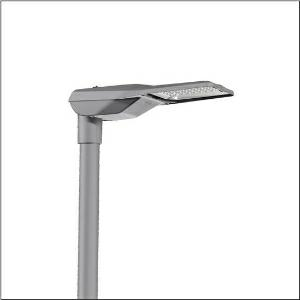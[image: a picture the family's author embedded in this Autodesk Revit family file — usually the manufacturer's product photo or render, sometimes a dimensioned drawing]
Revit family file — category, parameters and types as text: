
# Revit family: streetlight_sl_21_mini___p0_5a_5xe2v33s08gb_4fda
name_source: partatom
category: Lighting Fixtures
units: mm (PartAtom-declared; Revit-internal decimal feet)

## family parameters
Cut with Voids When Loaded = No
Host = Face
Light Source = No
Part Type = Normal
Room Calculation Point = No
Round Connector Dimension = Use Diameter
Shared = No

## types (1)
- --- (1 x LED, 5840 lm, 40.4 W, 3000K)
    Apparent Load = 40 VA
    CIE Flux Codes = 37 73 96 100 100
    Color Rendering = 70
    Color Temperature = 3000K
    Default Elevation = 1800 mm
    Description = Streetlight SL 21 mini, mast luminaire, primary light control with lens, of PMMA, primary optical cover: cover, of toughened safety glass, transparent, light distribution: P0.5a, light emission: direct distribution, primary light characteristic: asymmetric, installation type: post-top, side-entry, LED, High Power LED, rated luminous flux: 5.840lm, luminous efficacy: 145lm/W, light colour: 730, colour temperature: 3000K, control gear: D4i, control: pre-setting: logarithmic dimming characteristic, flexible luminous flux parameterisation, time-dependent luminous flux control, constant luminous flux control, overheat protection, mains connection: 220..240V, AC, 50/60Hz, start of lifetime: 40W, end of service life: 41W, reduction: 19W, luminaire housing, of diecast aluminium, powder-coated, Siteco® metallic grey (DB 702S), corrosivity category C5 mid according to DIN EN ISO 12944, multi-level sealing system, sealing non-destructively replaceable, inclination adjustable: 0°, 5°, 10°, 15°, please order mast flange separately, length: 628mm, width: 235mm, height: 110mm, mast flange for spigot size: 42mm (side-entry): 5XC10008XM4, 60/48mm (side-entry/post-top): 5XC10108XM2, 76/60mm (side-entry/post-top): 5XC10108XM1, mounting height: 4..8m, Smart Interface above, protection rating (complete): IP66, insulation class (complete): insulation class II (safety insulation), certification: CE, ENEC, ENEC+, VDE, impact resistance: IK10, permissible operating ambient temperature for outdoor applications: -40..+50°C, standard-compliant lighting for roads and squares, packaging unit: 1 piece

Light Distribution: P0.5a
    Height = 110 mm
    Lamp = 1 x LED
    Lamp Light Flux = 5840 lm
    Lamp Power = 40.4 W
    Lamp count = 1
    Length = 625 mm
    Luminous efficacy = 145 lm/W
    Manufacturer = Siteco
    ModVariant = No
    Model = 5XE2V33S08GB
    Number of Poles = 1
    OnlyDefault = Yes
    Power Factor = 1
    Product Name = Streetlight SL 21 mini | P0.5a
    Product group = mast luminaire | pylon top
    ProductGroupID = 6100
    Protection Class = Protection class II
    Protection Degree = IP 66
    RLX_Detail_Level = 1
    RLX_Emergency_Light_Flux = 0 lm
    RLX_Emergency_Type = 0
    RLX_Emergency_Type_DB = No
    RlxData = <blob elided: 25717 chars, md5=f428bb65>
    Socket = socket
    Standby Power = 0 W
    System Light Flux = 5840 lm
    System Power = 40 W
    Type Comments = factory setting: luminous flux: 100 % | dim-lin: 254 | 812 mA
    Type Image = l_1003515.jpg
    URL = http://relux.com
    VarID = @adj_069540
    Voltage = 0 V
    Weight = 0.00 kg
    Width = 234 mm

## geometry (parser evidence)
native form markers: Blend x4, Sweep x10
no freeform markers — native parametric forms only
